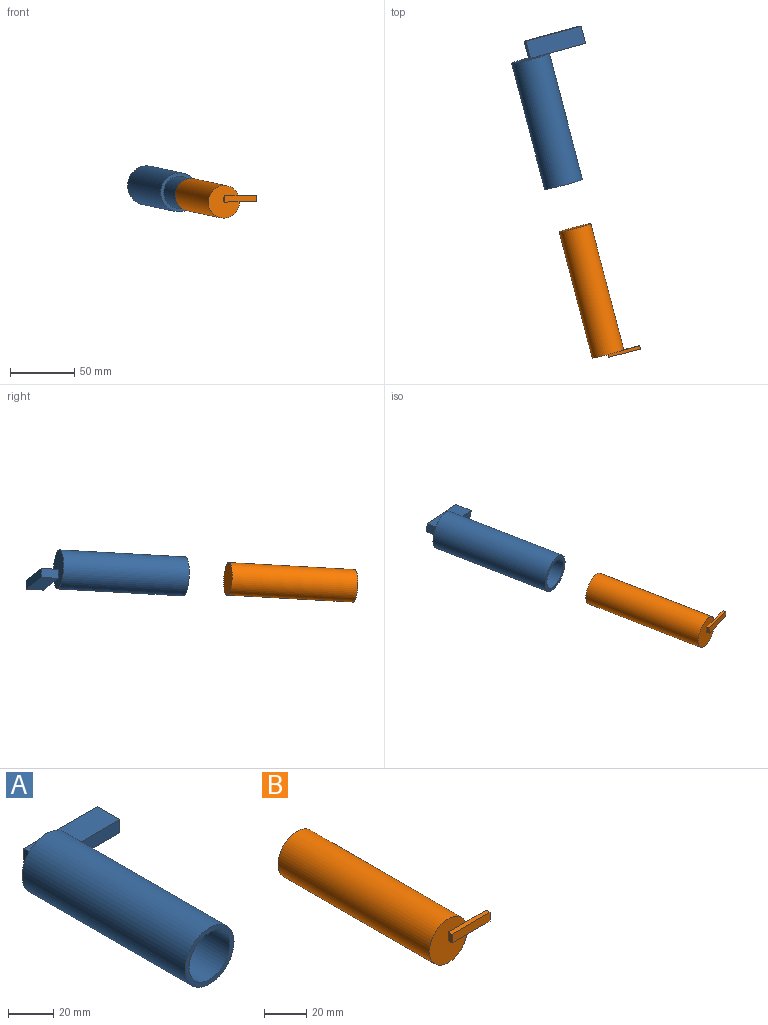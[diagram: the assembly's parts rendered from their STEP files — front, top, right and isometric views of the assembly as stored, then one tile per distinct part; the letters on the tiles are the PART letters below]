
ASSEMBLY  parts=2 mates=1
PART A: 11 faces, bbox 60.8x115.6x30.5 mm
  f0: cylinder r=15.24mm len=101.6mm, axis (0,1,0), area 9728.8mm2, adj f1,f2,f9
  f1: plane 30.48x30.48mm, normal (0,-1,0), area 223mm2, adj f0,f3
  f2: plane 30.48x30.48mm, normal (0,1,0), area 624.7mm2, adj f0,f5,f6,f7
  f3: cylinder r=12.7mm len=99.06mm, axis (0,1,0), area 7904.6mm2, adj f1,f4
  f4: plane 25.4x25.4mm, normal (0,-1,0), area 506.7mm2, adj f3
  f5: plane 45.53x14mm, normal (0,0,-1), area 637.3mm2, adj f2,f6,f8,f9,f10
  f6: plane 14x7.16mm, normal (-1,0,0), area 100.2mm2, adj f2,f5,f7,f10
  f7: plane 45.53x14mm, normal (0,0,1), area 637.3mm2, adj f2,f6,f8,f9,f10
  f8: plane 14x7.16mm, normal (1,0,0), area 100.2mm2, adj f5,f7,f9,f10
  f9: plane 32.08x7.16mm, normal (0,-1,0), area 221.1mm2, adj f0,f5,f7,f8
  f10: plane 45.53x7.16mm, normal (0,1,0), area 326.1mm2, adj f5,f6,f7,f8
PART B: 9 faces, bbox 38.1x104.1x25.4 mm
  f0: plane 25.4x25.4mm, normal (0,-1,0), area 444mm2, adj f1,f4,f5,f6
  f1: cylinder r=12.7mm len=101.6mm, axis (0,1,0), area 8107.3mm2, adj f0,f2,f3
  f2: plane 25.4x25.4mm, normal (0,1,0), area 506.7mm2, adj f1
  f3: plane 13.76x5.08mm, normal (0,1,0), area 66.3mm2, adj f1,f4,f6,f7
  f4: plane 25.4x2.54mm, normal (0,0,1), area 64.5mm2, adj f0,f3,f5,f7,f8
  f5: plane 5.08x2.54mm, normal (-1,0,0), area 12.9mm2, adj f0,f4,f6,f8
  f6: plane 25.4x2.54mm, normal (0,0,-1), area 64.5mm2, adj f0,f3,f5,f7,f8
  f7: plane 5.08x2.54mm, normal (1,0,0), area 12.9mm2, adj f3,f4,f6,f8
  f8: plane 25.4x5.08mm, normal (0,-1,0), area 129mm2, adj f4,f5,f6,f7
PLACE A rot(axis=(0.08,0.62,0.78),19.2deg) t=(-15.64,53.74,202.06)mm
PLACE B rot(axis=(0.21,0,0.98),15deg) t=(19.01,-78.47,194.69)mm
MATE cylindrical B.f1 <-> A.f0  axis (-0.25,0.97,0.05) through (19.01,-78.47,194.69)mm
